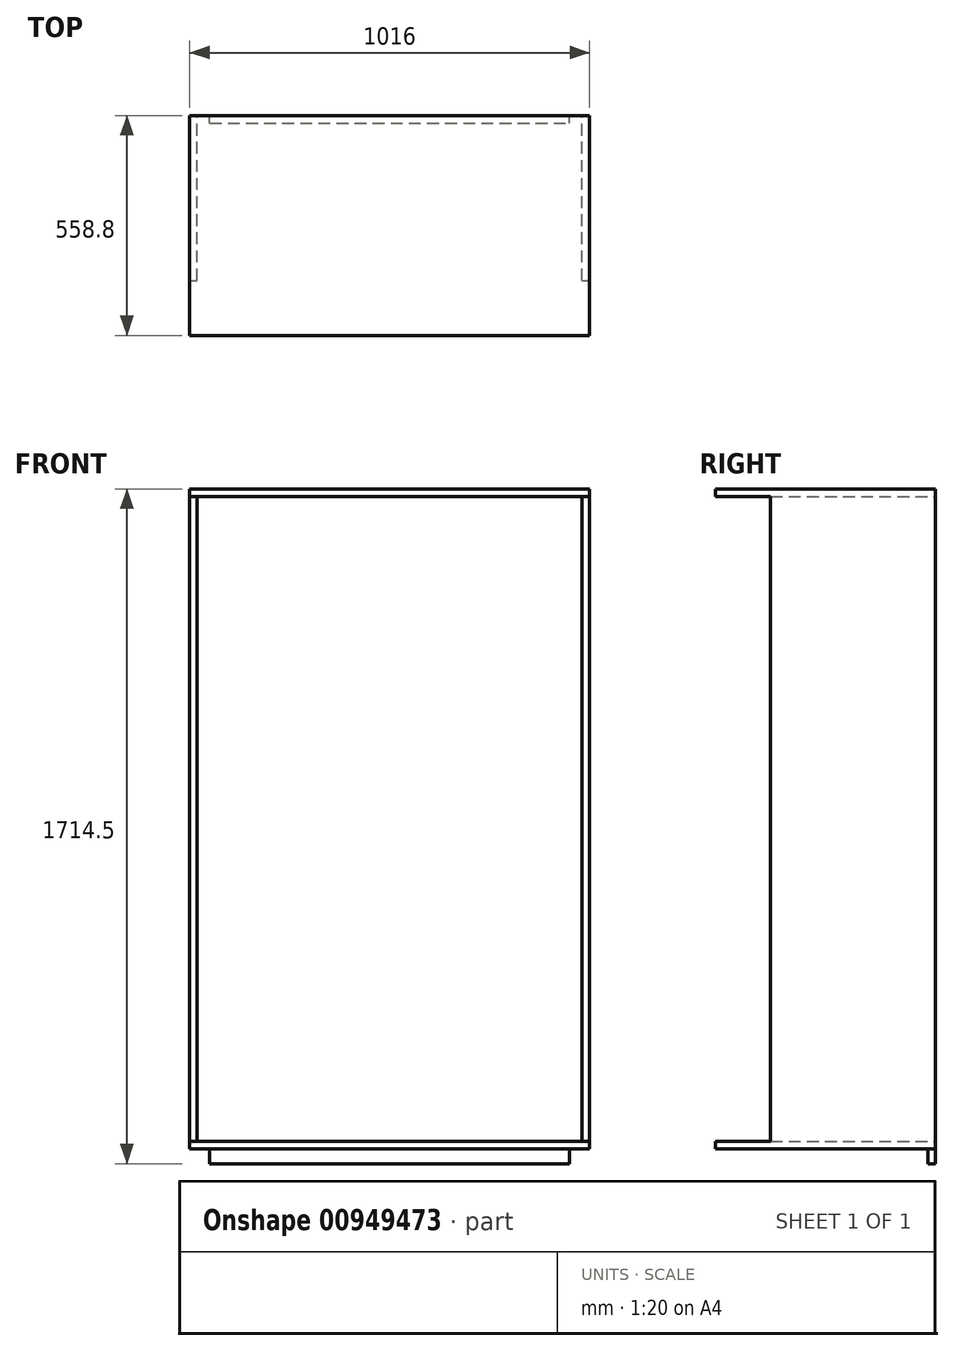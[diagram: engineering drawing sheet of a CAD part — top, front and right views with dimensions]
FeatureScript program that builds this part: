
annotation { "Feature Type Name" : "Feature", "Feature Type Description" : "" }
export const myFeature = defineFeature(function(context is Context, id is Id, definition is map)
    precondition{}
    {
        {
            var Q0;
            Q0=qCreatedBy(makeId("Front.planeOp"),FACE);
            var sketch = newSketch(context, id + "F0", { "sketchPlane" : qUnion([Q0])});
            skLineSegment(sketch, "E0.bottom", {"start": v(0, 0) * mm, "end": v(50.8, 0) * mm});
            skLineSegment(sketch, "E0.top", {"start": v(0, 1854.2) * mm, "end": v(1016, 1854.2) * mm});
            skLineSegment(sketch, "E0.left", {"start": v(0, 0) * mm, "end": v(0, 1854.2) * mm});
            skLineSegment(sketch, "E0.right", {"start": v(1016, 0) * mm, "end": v(1016, 1854.2) * mm});
            skLineSegment(sketch, "E1", {"start": v(19.05, 1758.95) * mm, "end": v(19.05, 120.65) * mm});
            skLineSegment(sketch, "E2", {"start": v(996.95, 1758.95) * mm, "end": v(996.95, 120.65) * mm});
            skLineSegment(sketch, "E3", {"start": v(0, 120.65) * mm, "end": v(1016, 120.65) * mm});
            skPoint(sketch, "E4.orphan", {"position": v(996.95, 0) * mm});
            skLineSegment(sketch, "E5", {"start": v(0, 101.6) * mm, "end": v(1016, 101.6) * mm});
            skLineSegment(sketch, "E6", {"start": v(50.8, 0) * mm, "end": v(50.8, 0) * mm});
            skLineSegment(sketch, "E7", {"start": v(50.8, 0) * mm, "end": v(50.8, 101.6) * mm});
            skLineSegment(sketch, "E8", {"start": v(0, 1758.95) * mm, "end": v(1016, 1758.95) * mm});
            skLineSegment(sketch, "E9", {"start": v(508, 1854.2) * mm, "end": v(508, 0) * mm, "construction": true});
            skLineSegment(sketch, "E10.MirrorCS", {"start": v(965.2, 0) * mm, "end": v(965.2, 101.6) * mm});
            skLineSegment(sketch, "E11.0", {"start": v(0, 1778) * mm, "end": v(1016, 1778) * mm});
            skLineSegment(sketch, "E12.trimOffspring", {"start": v(965.2, 0) * mm, "end": v(1016, 0) * mm});
            skLineSegment(sketch, "E13.bottom", {"start": v(50.8, 101.6) * mm, "end": v(965.2, 101.6) * mm});
            skLineSegment(sketch, "E13.top", {"start": v(50.8, 63.5) * mm, "end": v(965.2, 63.5) * mm});
            skLineSegment(sketch, "E13.left", {"start": v(50.8, 101.6) * mm, "end": v(50.8, 63.5) * mm});
            skLineSegment(sketch, "E13.right", {"start": v(965.2, 101.6) * mm, "end": v(965.2, 63.5) * mm});
            skSolve(sketch);
        }
        {
            var Q0;
            {var subQ0=sQuery(id+"F0.wireOp",EDGE,"E3");var subQ7=sQuery(id+"F0.wireOp",EDGE,"E0.left");var subQ8=makeQuery(id+"F0.imprint","INTERSECT",VERTEX,{"derivedFrom":[subQ7,subQ0]});Q0=makeQuery(id+"F0.imprint","IMPRINT",FACE,{"disambiguationData":[TD([[makeQuery(id+"F0.imprint","IMPRINT",EDGE,{"disambiguationData":[TD([[subQ8,1.0]])],"derivedFrom":subQ7}),-1.0]])]});}
            extrude(context, id + "F1", {"entities" : qUnion([Q0]), "depth" : 558.8 * mm, "offsetDistance" : 25.4 * mm});
        }
        {
            var Q0;
            {var subQ5=sQuery(id+"F0.wireOp",EDGE,"E2");Q0=makeQuery(id+"F0.imprint","IMPRINT",FACE,{"disambiguationData":[TD([[makeQuery(id+"F0.imprint","IMPRINT",EDGE,{"derivedFrom":subQ5}),1.0]])]});}
            var Q1;
            {var subQ5=sQuery(id+"F0.wireOp",EDGE,"E1");Q1=makeQuery(id+"F0.imprint","IMPRINT",FACE,{"disambiguationData":[TD([[makeQuery(id+"F0.imprint","IMPRINT",EDGE,{"derivedFrom":subQ5}),-1.0]])]});}
            extrude(context, id + "F2", {"entities" : qUnion([Q0, Q1]), "operationType" : NewBodyOperationType.ADD, "depth" : 419.1 * mm, "offsetDistance" : 25.4 * mm});
        }
        {
            var Q0;
            {var subQ5=sQuery(id+"F0.wireOp",EDGE,"E11.0");Q0=makeQuery(id+"F0.imprint","IMPRINT",FACE,{"disambiguationData":[TD([[makeQuery(id+"F0.imprint","IMPRINT",EDGE,{"derivedFrom":subQ5}),-1.0]])]});}
            extrude(context, id + "F3", {"entities" : qUnion([Q0]), "operationType" : NewBodyOperationType.ADD, "depth" : 558.8 * mm, "offsetDistance" : 25.4 * mm});
        }
        {
            var Q0;
            {var subQ5=sQuery(id+"F0.wireOp",EDGE,"E13.top");Q0=makeQuery(id+"F0.imprint","IMPRINT",FACE,{"disambiguationData":[TD([[makeQuery(id+"F0.imprint","IMPRINT",EDGE,{"derivedFrom":subQ5}),1.0]])]});}
            extrude(context, id + "F4", {"entities" : qUnion([Q0]), "operationType" : NewBodyOperationType.ADD, "depth" : 19.05 * mm, "offsetDistance" : 25.4 * mm});
        }
    });
